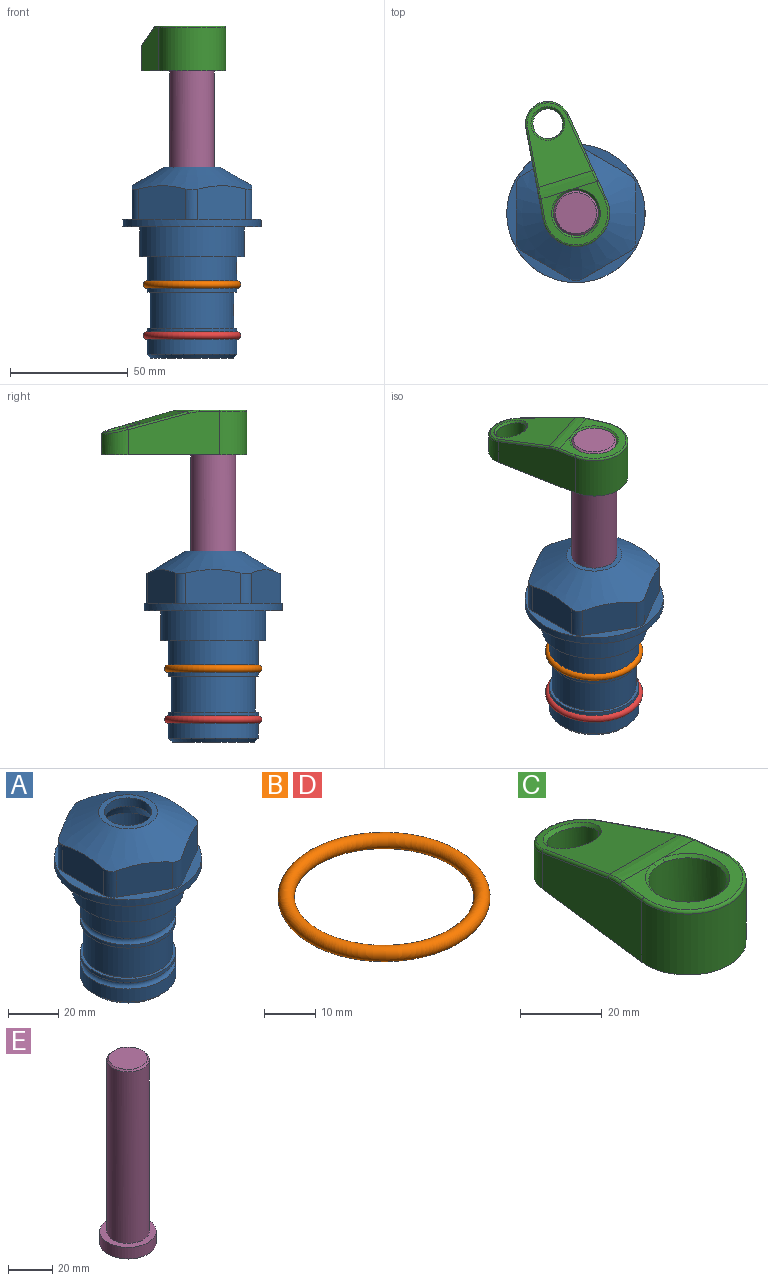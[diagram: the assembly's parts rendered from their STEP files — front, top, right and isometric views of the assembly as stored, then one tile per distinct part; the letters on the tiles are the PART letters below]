
ASSEMBLY  parts=5 mates=4
PART A: 36 faces, bbox 58.7x58.7x81 mm
  f0: cylinder r=17.78mm len=35.56mm, axis (0,0,1), area 1670.8mm2, adj f23,f24,f31
  f1: cylinder r=19.05mm len=38.1mm, axis (0,0,1), area 1191.9mm2, adj f26,f27,f30
  f2: plane 58.66x58.66mm, normal (0,0,-1), area 1150.6mm2, adj f3,f28
  f3: cylinder r=29.33mm len=58.66mm, axis (0,0,-1), area 585.1mm2, adj f2,f4
  f4: plane 58.66x58.66mm, normal (0,0,1), area 475.9mm2, adj f3,f5,f6,f7,f8,f9,f10,f11
  f5: plane 20.32x14.34mm, normal (-0.5,0.87,0), area 324.4mm2, adj f4,f15,f16,f17
  f6: plane 20.32x14.34mm, normal (0.5,0.87,0), area 324.4mm2, adj f4,f14,f15,f17
  f7: plane 23.48x14.34mm, normal (1,0,0), area 324.4mm2, adj f4,f13,f14,f17
  f8: plane 20.32x14.34mm, normal (0.5,-0.87,0), area 324.4mm2, adj f4,f12,f13,f17
  f9: plane 20.32x14.34mm, normal (-0.5,-0.87,0), area 324.4mm2, adj f4,f11,f12,f17
  f10: plane 23.48x14.34mm, normal (-1,0,0), area 324.4mm2, adj f4,f11,f16,f17
  f11: cylinder r=5.08mm len=12.85mm, axis (0,0,-1), area 67.2mm2, adj f4,f9,f10,f17
  f12: cylinder r=5.08mm len=12.85mm, axis (0,0,-1), area 67.2mm2, adj f4,f8,f9,f17
  f13: cylinder r=5.08mm len=12.85mm, axis (0,0,-1), area 67.2mm2, adj f4,f7,f8,f17
  f14: cylinder r=5.08mm len=12.85mm, axis (0,0,-1), area 67.2mm2, adj f4,f6,f7,f17
  f15: cylinder r=5.08mm len=12.85mm, axis (0,0,-1), area 67.2mm2, adj f4,f5,f6,f17
  f16: cylinder r=5.08mm len=12.85mm, axis (0,0,-1), area 67.2mm2, adj f4,f5,f10,f17
  f17: cone r=11.73mm half-angle=60deg, axis (0,0,-1), area 2071.8mm2, adj f5,f6,f7,f8,f9,f10,f11,f12
  f18: plane 23.46x23.46mm, normal (0,0,1), area 147.4mm2, adj f17,f35
  f19: plane 34.93x34.93mm, normal (0,0,-1), area 958mm2, adj f29
  f20: cylinder r=19.05mm len=38.1mm, axis (0,0,1), area 760.1mm2, adj f21,f29
  f21: torus R=19.05mm, axis (0,0,1), area 565.3mm2, adj f20,f22
  f22: cylinder r=19.05mm len=38.1mm, axis (0,0,1), area 190mm2, adj f21,f23
  f23: plane 38.1x38.1mm, normal (0,0,1), area 146.9mm2, adj f0,f22
  f24: plane 38.1x38.1mm, normal (0,0,-1), area 146.9mm2, adj f0,f25
  f25: cylinder r=19.05mm len=38.1mm, axis (0,0,1), area 190mm2, adj f24,f26
  f26: torus R=19.05mm, axis (0,0,1), area 565.3mm2, adj f1,f25
  f27: plane 44.45x44.45mm, normal (0,0,-1), area 411.7mm2, adj f1,f28
  f28: cylinder r=22.23mm len=44.45mm, axis (0,0,1), area 1773.5mm2, adj f2,f27
  f29: cone r=19.05mm half-angle=45deg, axis (0,0,1), area 257.5mm2, adj f19,f20
  f30: cylinder r=3.17mm len=6.75mm, axis (-1,0,0), area 128mm2, adj f1,f33
  f31: cylinder r=3.17mm len=6.35mm, axis (-1,0,0), area 102.5mm2, adj f0,f33
  f32: plane 25.4x25.4mm, normal (0,0,1), area 506.7mm2, adj f33
  f33: cylinder r=12.7mm len=66.42mm, axis (0,0,-1), area 5236.2mm2, adj f30,f31,f32,f34
  f34: cone r=9.53mm half-angle=30deg, axis (0,0,-1), area 443.4mm2, adj f33,f35
  f35: cylinder r=9.53mm len=19.05mm, axis (0,0,-1), area 240.9mm2, adj f18,f34
PART B: 1 faces, bbox 44.7x44.7x3.2 mm
  f0: torus R=19.05mm, axis (0,0,1), area 1193.9mm2
PART C: 31 faces, bbox 31.7x65.5x19.8 mm
  f0: plane 39.12x18.26mm, normal (0.99,0.12,0), area 612.2mm2, adj f1,f4,f7,f11,f13,f15
  f1: cylinder r=9.53mm len=18.91mm, axis (0,0,-1), area 296.1mm2, adj f0,f2,f7,f17
  f2: plane 39.12x18.26mm, normal (-0.99,0.12,0), area 612.2mm2, adj f1,f4,f7,f12,f14,f16
  f3: cylinder r=6.35mm len=12.7mm, axis (0,0,-1), area 362.4mm2, adj f7,f18
  f4: cylinder r=14.29mm len=28.58mm, axis (0,0,-1), area 882.2mm2, adj f0,f2,f7,f10
  f5: cylinder r=9.53mm len=19.05mm, axis (0,0,-1), area 1092.6mm2, adj f7,f19,f20
  f6: plane 26.99x23.69mm, normal (0,0,1), area 216.2mm2, adj f9,f10,f11,f12,f19
  f7: plane 63.5x28.58mm, normal (0,0,-1), area 661.8mm2, adj f0,f1,f2,f3,f4,f5,f22,f23
  f8: plane 33.52x23.6mm, normal (0,0.26,0.97), area 486mm2, adj f9,f15,f16,f17,f18
  f9: cylinder r=19.05mm len=24.72mm, axis (1,0,0), area 120.4mm2, adj f6,f8,f13,f14,f20
  f10: torus R=13.49mm, axis (0,0,1), area 59mm2, adj f4,f6,f11,f12
  f11: cylinder r=0.79mm len=8.67mm, axis (0.12,-0.99,0), area 10.8mm2, adj f0,f6,f10,f13
  f12: cylinder r=0.79mm len=8.67mm, axis (0.12,0.99,0), area 10.8mm2, adj f2,f6,f10,f14
  f13: bspline ~4.95x1.42mm, area 6.1mm2, adj f0,f9,f11,f15
  f14: bspline ~4.95x1.42mm, area 6.1mm2, adj f2,f9,f12,f16
  f15: cylinder r=0.79mm len=25.95mm, axis (0.12,-0.96,0.26), area 32.9mm2, adj f0,f8,f13,f17
  f16: cylinder r=0.79mm len=25.95mm, axis (0.12,0.96,-0.26), area 32.9mm2, adj f2,f8,f14,f17
  f17: bspline ~18.91x8.38mm, area 30mm2, adj f1,f8,f15,f16
  f18: bspline ~14.29x14.29mm, area 48.3mm2, adj f3,f8
  f19: cone r=9.53mm half-angle=45deg, axis (0,0,1), area 66.5mm2, adj f5,f6,f20
  f20: bspline ~3.22x0.96mm, area 3.5mm2, adj f5,f9,f19
  f21: plane 2.75x2.72mm, normal (0,0,-1), area 2.9mm2, adj f23,f25,f28
  f22: plane 23.05x15.88mm, normal (-0.99,-0.12,0), area 323.6mm2, adj f7,f25,f26,f27,f28,f29
  f23: plane 23.05x15.88mm, normal (0.99,-0.12,0), area 323.6mm2, adj f7,f21,f25,f27,f28,f30
  f24: cylinder r=9.53mm len=10.69mm, axis (0,0,-1), area 114.7mm2, adj f7,f27,f29,f30
  f25: cylinder r=12.7mm len=20.59mm, axis (0,0,-1), area 381.1mm2, adj f7,f21,f22,f23,f26,f28
  f26: plane 2.75x2.72mm, normal (0,0,-1), area 2.9mm2, adj f22,f25,f28
  f27: plane 19.72x18.37mm, normal (0,-0.26,-0.97), area 291.8mm2, adj f22,f23,f24,f28,f29,f30
  f28: cylinder r=15.88mm len=19.92mm, axis (1,0,0), area 54.8mm2, adj f21,f22,f23,f25,f26,f27
  f29: cylinder r=1.59mm len=11mm, axis (0,0,-1), area 34.7mm2, adj f7,f22,f24,f27
  f30: cylinder r=1.59mm len=11mm, axis (0,0,-1), area 34.7mm2, adj f7,f23,f24,f27
PART D: same geometry as B
PART E: 6 faces, bbox 25.4x25.4x101.6 mm
  f0: plane 17.46x17.46mm, normal (0,0,1), area 239.5mm2, adj f5
  f1: plane 25.4x25.4mm, normal (0,0,-1), area 506.7mm2, adj f2
  f2: cylinder r=12.7mm len=25.4mm, axis (0,0,1), area 506.7mm2, adj f1,f3
  f3: plane 25.4x25.4mm, normal (0,0,1), area 221.7mm2, adj f2,f4
  f4: cylinder r=9.53mm len=94.46mm, axis (0,0,1), area 5653mm2, adj f3,f5
  f5: cone r=8.73mm half-angle=45deg, axis (0,0,-1), area 64.4mm2, adj f0,f4
PLACE A t=(-8.27,-8.78,4.93)mm fixed
PLACE B t=(-8.27,-8.78,4.93)mm
PLACE C rot(axis=(0,0,1),17.4deg) t=(-8.27,-8.78,26.65)mm
PLACE D t=(-8.27,-8.78,-16.66)mm
PLACE E rot(axis=(0,0,1),17.4deg) t=(-8.27,-8.78,26.65)mm
MATE cylindrical E.f2 <-> A.f0  axis (0,0,-1) through (-8.27,-8.78,-11.45)mm
MATE fastened D.f0 <-> A.f0  axis (0,0,1) through (-8.27,-8.78,-41.18)mm
MATE fastened B.f0 <-> A.f0  axis (0,0,1) through (-8.27,-8.78,-19.59)mm
MATE fastened C.f4 <-> E.f2  axis (0,0,1) through (-8.27,-8.78,90.15)mm
